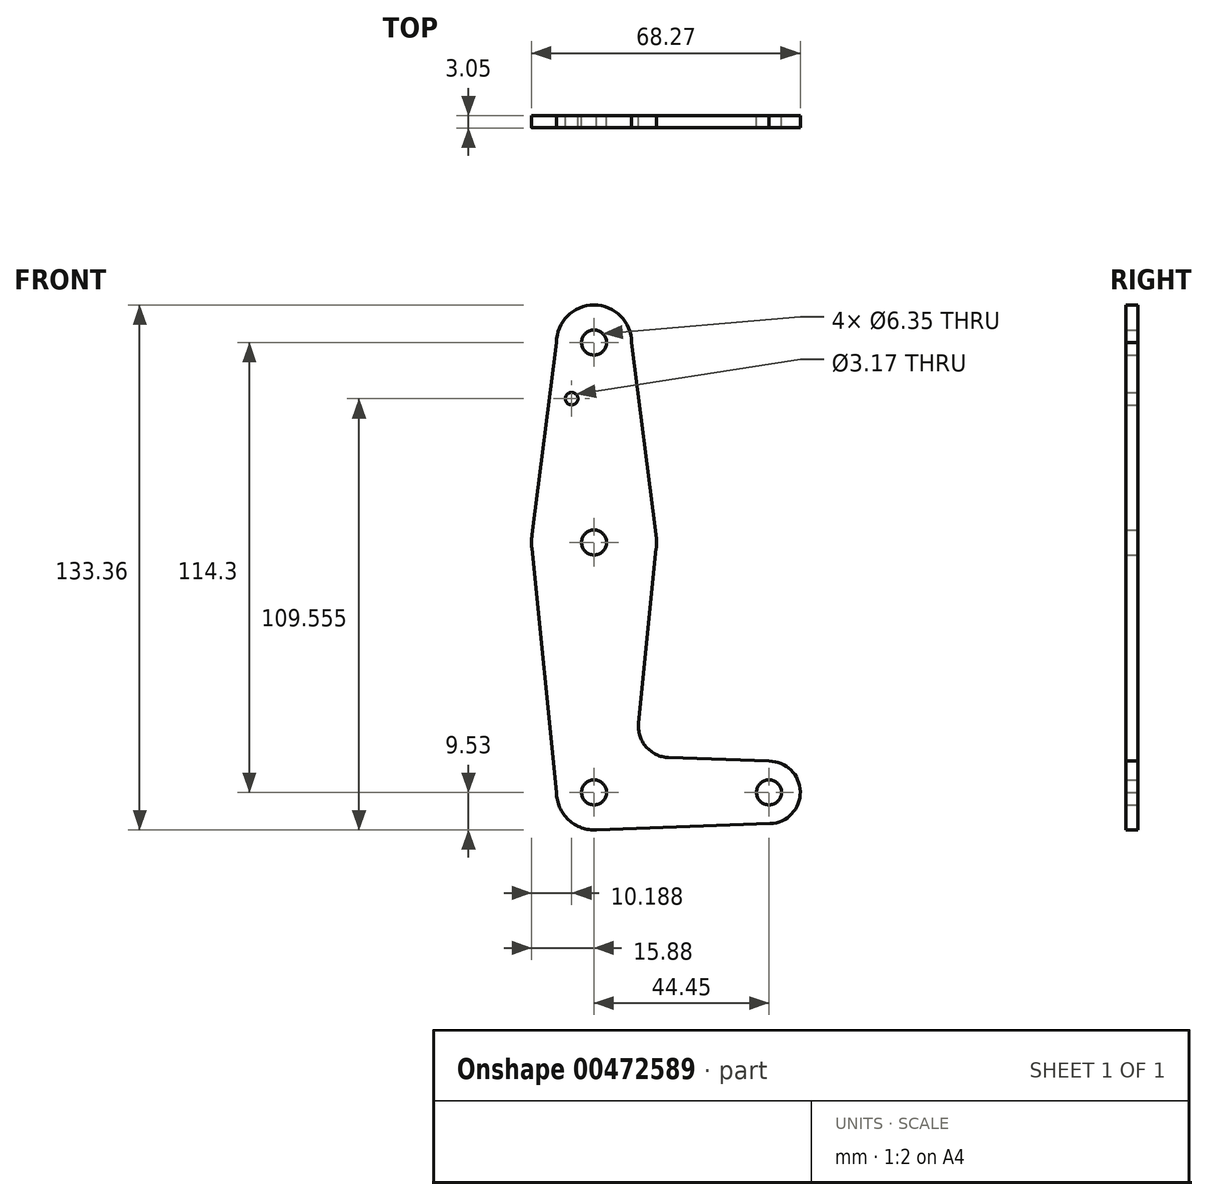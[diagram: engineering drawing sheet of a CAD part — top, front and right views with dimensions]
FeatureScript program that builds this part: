
annotation { "Feature Type Name" : "Feature", "Feature Type Description" : "" }
export const myFeature = defineFeature(function(context is Context, id is Id, definition is map)
    precondition{}
    {
        {
            var Q0;
            Q0=qCreatedBy(makeId("Front.planeOp"),FACE);
            var sketch = newSketch(context, id + "F0", { "sketchPlane" : qUnion([Q0])});
            skLineSegment(sketch, "E0", {"start": v(0, 114.3) * mm, "end": v(0, 0) * mm, "construction": true});
            skLineSegment(sketch, "E1", {"start": v(0, 0) * mm, "end": v(44.45, 0) * mm, "construction": true});
            skCircle(sketch, "E2", {"center": v(0, 63.5) * mm, "radius": 15.88 * mm});
            skCircle(sketch, "E3", {"center": v(0, 114.3) * mm, "radius": 9.53 * mm});
            skCircle(sketch, "E4", {"center": v(0, 0) * mm, "radius": 9.53 * mm});
            skCircle(sketch, "E5", {"center": v(44.45, 0) * mm, "radius": 7.94 * mm});
            skLineSegment(sketch, "E6", {"start": v(-9.53, 114.3) * mm, "end": v(-15.75, 65.5) * mm});
            skLineSegment(sketch, "E7", {"start": v(9.53, 114.3) * mm, "end": v(15.75, 65.5) * mm});
            skCircle(sketch, "E8", {"center": v(-5.7, 100.03) * mm, "radius": 1.59 * mm});
            skLineSegment(sketch, "E9", {"start": v(0, -9.53) * mm, "end": v(44.73, -7.93) * mm});
            skCircle(sketch, "E10", {"center": v(0, 114.3) * mm, "radius": 3.18 * mm});
            skCircle(sketch, "E11", {"center": v(0, 63.5) * mm, "radius": 3.18 * mm});
            skCircle(sketch, "E12", {"center": v(0, 0) * mm, "radius": 3.18 * mm});
            skCircle(sketch, "E13", {"center": v(44.45, 0) * mm, "radius": 3.18 * mm});
            skLineSegment(sketch, "E14", {"start": v(44.45, 7.94) * mm, "end": v(18.93, 8.85) * mm});
            skLineSegment(sketch, "E15", {"start": v(11.3, 17.6) * mm, "end": v(15.8, 61.9) * mm});
            skLineSegment(sketch, "E16", {"start": v(-9.53, 0) * mm, "end": v(-15.8, 61.9) * mm});
            skPoint(sketch, "E17.newPointB", {"position": v(0, 9.53) * mm});
            skArc(sketch, "E17.filletArc", {"start": v(11.3, 17.6) * mm, "mid": v(13.23, 11.57) * mm, "end": v(18.93, 8.85) * mm});
            skSolve(sketch);
        }
        {
            var Q0;
            Q0 = qSketchRegion(id + "F0", true);
            extrude(context, id + "F1", {"entities" : qUnion([Q0]), "depth" : 3.05 * mm});
        }
    });
